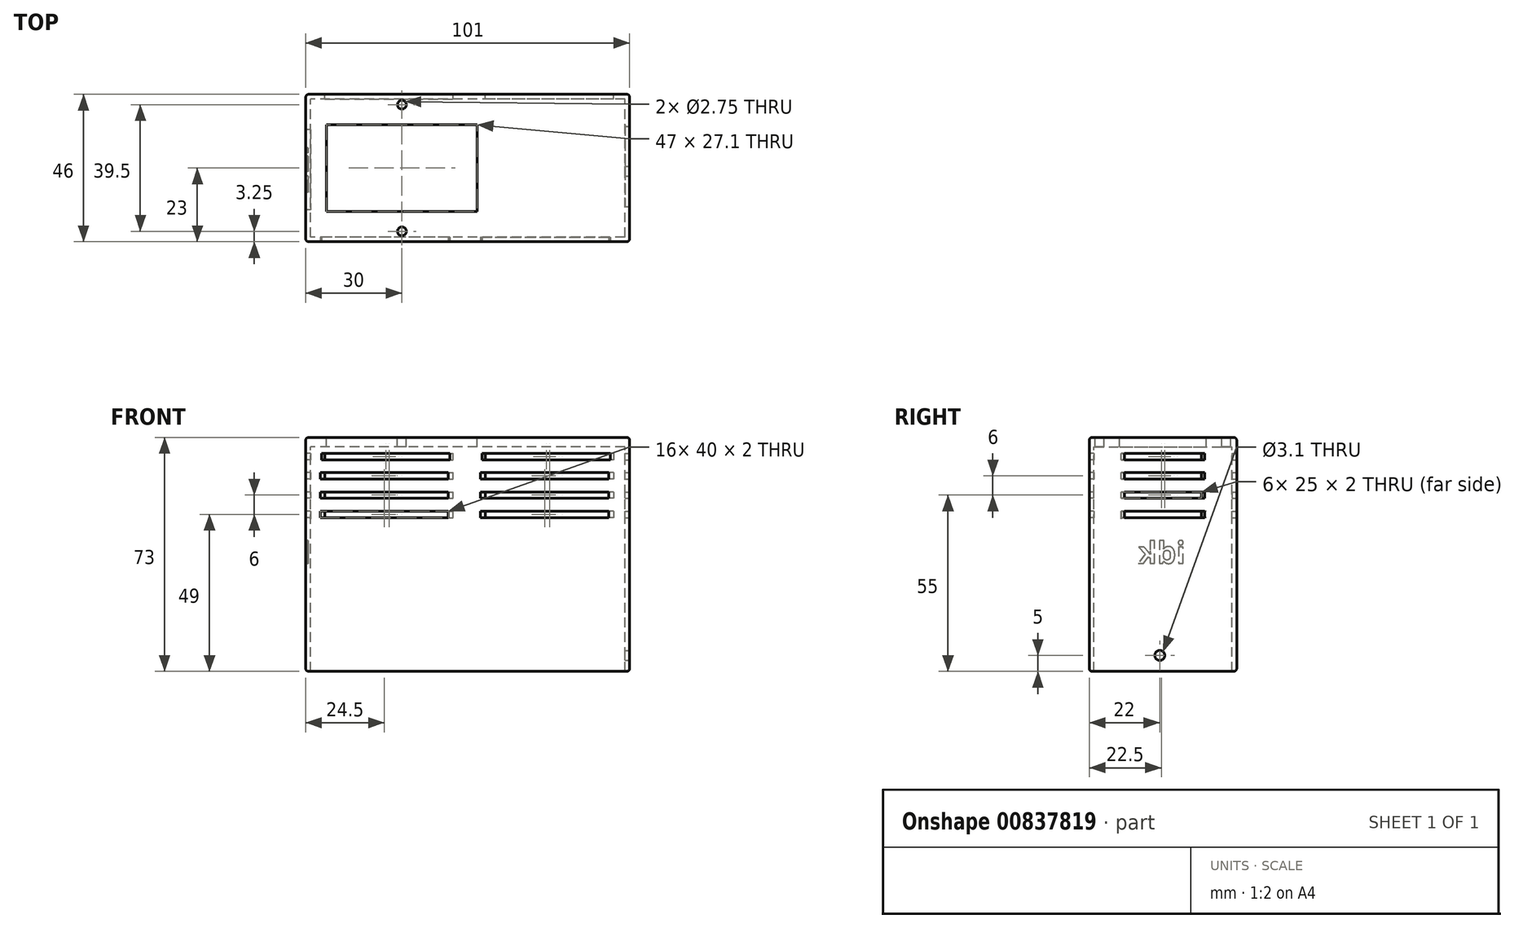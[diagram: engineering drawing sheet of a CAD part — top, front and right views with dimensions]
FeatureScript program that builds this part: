
annotation { "Feature Type Name" : "Feature", "Feature Type Description" : "" }
export const myFeature = defineFeature(function(context is Context, id is Id, definition is map)
    precondition{}
    {
        {
            var Q0;
            Q0=qCreatedBy(makeId("Top.planeOp"),FACE);
            var sketch = newSketch(context, id + "F0", { "sketchPlane" : qUnion([Q0])});
            skLineSegment(sketch, "E0.bottom", {"start": v(49, -21.5) * mm, "end": v(-49, -21.5) * mm});
            skLineSegment(sketch, "E0.top", {"start": v(49, 21.5) * mm, "end": v(-49, 21.5) * mm});
            skLineSegment(sketch, "E0.left", {"start": v(49, -21.5) * mm, "end": v(49, 21.5) * mm});
            skLineSegment(sketch, "E0.right", {"start": v(-49, -21.5) * mm, "end": v(-49, 21.5) * mm});
            skPoint(sketch, "E0.middle", {"position": v(0, 0) * mm});
            skLineSegment(sketch, "E1.bottom", {"start": v(50.5, -23) * mm, "end": v(-50.5, -23) * mm});
            skLineSegment(sketch, "E1.top", {"start": v(50.5, 23) * mm, "end": v(-50.5, 23) * mm});
            skLineSegment(sketch, "E1.left", {"start": v(50.5, -23) * mm, "end": v(50.5, 23) * mm});
            skLineSegment(sketch, "E1.right", {"start": v(-50.5, -23) * mm, "end": v(-50.5, 23) * mm});
            skLineSegment(sketch, "E2.bottom", {"start": v(3, -13.55) * mm, "end": v(-44, -13.55) * mm});
            skLineSegment(sketch, "E2.top", {"start": v(3, 13.55) * mm, "end": v(-44, 13.55) * mm});
            skLineSegment(sketch, "E2.left", {"start": v(3, -13.55) * mm, "end": v(3, 13.55) * mm});
            skLineSegment(sketch, "E2.right", {"start": v(-44, -13.55) * mm, "end": v(-44, 13.55) * mm});
            skPoint(sketch, "E2.middle", {"position": v(-20.5, 0) * mm});
            skLineSegment(sketch, "E3.bottom", {"start": v(39, -10) * mm, "end": v(26, -10) * mm});
            skLineSegment(sketch, "E3.top", {"start": v(39, 10) * mm, "end": v(26, 10) * mm});
            skLineSegment(sketch, "E3.left", {"start": v(39, -10) * mm, "end": v(39, 10) * mm});
            skLineSegment(sketch, "E3.right", {"start": v(26, -10) * mm, "end": v(26, 10) * mm});
            skPoint(sketch, "E3.middle", {"position": v(32.5, 0) * mm});
            skCircle(sketch, "E4", {"center": v(-20.5, -19.75) * mm, "radius": 1.38 * mm});
            skCircle(sketch, "E5", {"center": v(-20.5, 19.75) * mm, "radius": 1.38 * mm});
            skSolve(sketch);
        }
        {
            var Q0;
            Q0=makeQuery(id+"F0.imprint","IMPRINT",FACE,{"disambiguationData":[TD([[makeQuery(id+"F0.imprint","IMPRINT",EDGE,{"derivedFrom":sQuery(id+"F0.wireOp",EDGE,"E0.bottom")}),1.0]])]});
            extrude(context, id + "F1", {"entities" : qUnion([Q0]), "oppositeDirection" : true, "depth" : 73 * mm, "offsetDistance" : 25 * mm});
        }
        {
            var Q0;
            Q0=makeQuery(id+"F0.imprint","IMPRINT",FACE,{"disambiguationData":[TD([[makeQuery(id+"F0.imprint","IMPRINT",EDGE,{"derivedFrom":sQuery(id+"F0.wireOp",EDGE,"E0.bottom")}),-1.0]])]});
            extrude(context, id + "F2", {"entities" : qUnion([Q0]), "operationType" : NewBodyOperationType.ADD, "oppositeDirection" : true, "depth" : 3 * mm, "offsetDistance" : 25 * mm});
        }
        {
            var Q0;
            Q0=qCreatedBy(makeId("Right.planeOp"),FACE);
            cPlane(context, id + "F3", {"entities" : qUnion([Q0]), "cplaneType" : CPlaneType.OFFSET, "offset" : 49 * mm, "width" : 150 * mm, "height" : 150 * mm});
        }
        {
            var Q0;
            Q0=makeQuery(id+"F1.opExtrude","SWEPT_FACE",FACE,{"disambiguationData":[OSD([sQuery(id+"F0.wireOp",EDGE,"E1.left")])]});
            var sketch = newSketch(context, id + "F4", { "sketchPlane" : qUnion([Q0])});
            skCircle(sketch, "E6", {"center": v(-1, -68) * mm, "radius": 1.55 * mm});
            skSolve(sketch);
        }
        {
            var Q0;
            Q0=makeQuery(id+"F4.imprint","IMPRINT",FACE,{"disambiguationData":[TD([[makeQuery(id+"F4.imprint","IMPRINT",EDGE,{"derivedFrom":sQuery(id+"F4.wireOp",EDGE,"E6")}),1.0]])]});
            extrude(context, id + "F5", {"entities" : qUnion([Q0]), "operationType" : NewBodyOperationType.REMOVE, "oppositeDirection" : true, "depth" : 3 * mm, "offsetDistance" : 25 * mm});
        }
        {
            var Q0;
            Q0=makeQuery(id+"F1.opExtrude","CAP_EDGE",EDGE,{"disambiguationData":[OSD([sQuery(id+"F0.wireOp",EDGE,"E1.bottom")])],"isStart":false});
            var Q1;
            Q1=makeQuery(id+"F1.opExtrude","CAP_EDGE",EDGE,{"disambiguationData":[OSD([sQuery(id+"F0.wireOp",EDGE,"E1.left")])],"isStart":false});
            var Q2;
            Q2=makeQuery(id+"F1.opExtrude","CAP_EDGE",EDGE,{"disambiguationData":[OSD([sQuery(id+"F0.wireOp",EDGE,"E1.top")])],"isStart":false});
            var Q3;
            Q3=makeQuery(id+"F1.opExtrude","CAP_EDGE",EDGE,{"disambiguationData":[OSD([sQuery(id+"F0.wireOp",EDGE,"E1.right")])],"isStart":false});
            var Q4;
            Q4=makeQuery(id+"F1.opExtrude","SWEPT_EDGE",EDGE,{"disambiguationData":[OSD([sQuery(id+"F0.wireOp",EDGE,"E1.bottom"),sQuery(id+"F0.wireOp",EDGE,"E1.right")])]});
            var Q5;
            Q5=makeQuery(id+"F1.opExtrude","SWEPT_EDGE",EDGE,{"disambiguationData":[OSD([sQuery(id+"F0.wireOp",EDGE,"E1.top"),sQuery(id+"F0.wireOp",EDGE,"E1.right")])]});
            var Q6;
            Q6=makeQuery(id+"F1.opExtrude","SWEPT_EDGE",EDGE,{"disambiguationData":[OSD([sQuery(id+"F0.wireOp",EDGE,"E1.bottom"),sQuery(id+"F0.wireOp",EDGE,"E1.left")])]});
            var Q7;
            Q7=makeQuery(id+"F1.opExtrude","SWEPT_EDGE",EDGE,{"disambiguationData":[OSD([sQuery(id+"F0.wireOp",EDGE,"E1.top"),sQuery(id+"F0.wireOp",EDGE,"E1.left")])]});
            var Q8;
            Q8=makeQuery(id+"F1.opExtrude","CAP_EDGE",EDGE,{"disambiguationData":[OSD([sQuery(id+"F0.wireOp",EDGE,"E1.bottom")])],"isStart":true});
            var Q9;
            Q9=makeQuery(id+"F1.opExtrude","CAP_EDGE",EDGE,{"disambiguationData":[OSD([sQuery(id+"F0.wireOp",EDGE,"E1.left")])],"isStart":true});
            var Q10;
            Q10=makeQuery(id+"F1.opExtrude","CAP_EDGE",EDGE,{"disambiguationData":[OSD([sQuery(id+"F0.wireOp",EDGE,"E1.top")])],"isStart":true});
            var Q11;
            Q11=makeQuery(id+"F1.opExtrude","CAP_EDGE",EDGE,{"disambiguationData":[OSD([sQuery(id+"F0.wireOp",EDGE,"E1.right")])],"isStart":true});
            var Q12;
            Q12=makeQuery(id+"F5.boolean.opBoolean","COPY",EDGE,{"derivedFrom":makeQuery(id+"F5.opExtrude","CAP_EDGE",EDGE,{"disambiguationData":[OSD([sQuery(id+"F4.wireOp",EDGE,"E6")])],"isStart":true})});
            fillet(context, id + "F6", {"entities" : qUnion([Q0, Q1, Q2, Q3, Q4, Q5, Q6, Q7, Q8, Q9, Q10, Q11, Q12]), "radius" : 1 * mm, "tangentPropagation" : true, "allowEdgeOverflow" : false});
        }
        {
            var Q0;
            Q0=makeQuery(id+"F1.opExtrude","SWEPT_FACE",FACE,{"disambiguationData":[OSD([sQuery(id+"F0.wireOp",EDGE,"E1.bottom")])]});
            var sketch = newSketch(context, id + "F7", { "sketchPlane" : qUnion([Q0])});
            skLineSegment(sketch, "E7.bottom", {"start": v(44.5, -7) * mm, "end": v(4.5, -7) * mm});
            skLineSegment(sketch, "E7.top", {"start": v(44.5, -5) * mm, "end": v(4.5, -5) * mm});
            skLineSegment(sketch, "E7.left", {"start": v(44.5, -7) * mm, "end": v(44.5, -5) * mm});
            skLineSegment(sketch, "E7.right", {"start": v(4.5, -7) * mm, "end": v(4.5, -5) * mm});
            skPoint(sketch, "E7.middle", {"position": v(24.5, -6) * mm});
            skLineSegment(sketch, "E8.bottom", {"start": v(-45.5, -5) * mm, "end": v(-5.5, -5) * mm});
            skLineSegment(sketch, "E8.top", {"start": v(-45.5, -7) * mm, "end": v(-5.5, -7) * mm});
            skLineSegment(sketch, "E8.left", {"start": v(-45.5, -5) * mm, "end": v(-45.5, -7) * mm});
            skLineSegment(sketch, "E8.right", {"start": v(-5.5, -5) * mm, "end": v(-5.5, -7) * mm});
            skPoint(sketch, "E8.middle", {"position": v(-25.5, -6) * mm});
            skLineSegment(sketch, "E9.bottom", {"start": v(44, -13) * mm, "end": v(4, -13) * mm});
            skLineSegment(sketch, "E9.top", {"start": v(44, -11) * mm, "end": v(4, -11) * mm});
            skLineSegment(sketch, "E9.left", {"start": v(44, -13) * mm, "end": v(44, -11) * mm});
            skLineSegment(sketch, "E9.right", {"start": v(4, -13) * mm, "end": v(4, -11) * mm});
            skPoint(sketch, "E9.middle", {"position": v(24, -12) * mm});
            skLineSegment(sketch, "E10.bottom", {"start": v(-46, -11) * mm, "end": v(-6, -11) * mm});
            skLineSegment(sketch, "E10.top", {"start": v(-46, -13) * mm, "end": v(-6, -13) * mm});
            skLineSegment(sketch, "E10.left", {"start": v(-46, -11) * mm, "end": v(-46, -13) * mm});
            skLineSegment(sketch, "E10.right", {"start": v(-6, -11) * mm, "end": v(-6, -13) * mm});
            skPoint(sketch, "E10.middle", {"position": v(-26, -12) * mm});
            skLineSegment(sketch, "E11.bottom", {"start": v(44, -19) * mm, "end": v(4, -19) * mm});
            skLineSegment(sketch, "E11.top", {"start": v(44, -17) * mm, "end": v(4, -17) * mm});
            skLineSegment(sketch, "E11.left", {"start": v(44, -19) * mm, "end": v(44, -17) * mm});
            skLineSegment(sketch, "E11.right", {"start": v(4, -19) * mm, "end": v(4, -17) * mm});
            skPoint(sketch, "E11.middle", {"position": v(24, -18) * mm});
            skLineSegment(sketch, "E12.bottom", {"start": v(-46, -17) * mm, "end": v(-6, -17) * mm});
            skLineSegment(sketch, "E12.top", {"start": v(-46, -19) * mm, "end": v(-6, -19) * mm});
            skLineSegment(sketch, "E12.left", {"start": v(-46, -17) * mm, "end": v(-46, -19) * mm});
            skLineSegment(sketch, "E12.right", {"start": v(-6, -17) * mm, "end": v(-6, -19) * mm});
            skPoint(sketch, "E12.middle", {"position": v(-26, -18) * mm});
            skLineSegment(sketch, "E13.bottom", {"start": v(44, -25) * mm, "end": v(4, -25) * mm});
            skLineSegment(sketch, "E13.top", {"start": v(44, -23) * mm, "end": v(4, -23) * mm});
            skLineSegment(sketch, "E13.left", {"start": v(44, -25) * mm, "end": v(44, -23) * mm});
            skLineSegment(sketch, "E13.right", {"start": v(4, -25) * mm, "end": v(4, -23) * mm});
            skPoint(sketch, "E13.middle", {"position": v(24, -24) * mm});
            skLineSegment(sketch, "E14.bottom", {"start": v(-46, -23) * mm, "end": v(-6, -23) * mm});
            skLineSegment(sketch, "E14.top", {"start": v(-46, -25) * mm, "end": v(-6, -25) * mm});
            skLineSegment(sketch, "E14.left", {"start": v(-46, -23) * mm, "end": v(-46, -25) * mm});
            skLineSegment(sketch, "E14.right", {"start": v(-6, -23) * mm, "end": v(-6, -25) * mm});
            skPoint(sketch, "E14.middle", {"position": v(-26, -24) * mm});
            skSolve(sketch);
        }
        {
            var Q0;
            Q0=makeQuery(id+"F1.opExtrude","SWEPT_FACE",FACE,{"disambiguationData":[OSD([sQuery(id+"F0.wireOp",EDGE,"E1.top")])]});
            var sketch = newSketch(context, id + "F8", { "sketchPlane" : qUnion([Q0])});
            skLineSegment(sketch, "E15.bottom", {"start": v(44.5, -7) * mm, "end": v(4.5, -7) * mm});
            skLineSegment(sketch, "E15.top", {"start": v(44.5, -5) * mm, "end": v(4.5, -5) * mm});
            skLineSegment(sketch, "E15.left", {"start": v(44.5, -7) * mm, "end": v(44.5, -5) * mm});
            skLineSegment(sketch, "E15.right", {"start": v(4.5, -7) * mm, "end": v(4.5, -5) * mm});
            skPoint(sketch, "E15.middle", {"position": v(24.5, -6) * mm});
            skLineSegment(sketch, "E16.bottom", {"start": v(-45.5, -5) * mm, "end": v(-5.5, -5) * mm});
            skLineSegment(sketch, "E16.top", {"start": v(-45.5, -7) * mm, "end": v(-5.5, -7) * mm});
            skLineSegment(sketch, "E16.left", {"start": v(-45.5, -5) * mm, "end": v(-45.5, -7) * mm});
            skLineSegment(sketch, "E16.right", {"start": v(-5.5, -5) * mm, "end": v(-5.5, -7) * mm});
            skPoint(sketch, "E16.middle", {"position": v(-25.5, -6) * mm});
            skLineSegment(sketch, "E17.bottom", {"start": v(44.5, -13) * mm, "end": v(4.5, -13) * mm});
            skLineSegment(sketch, "E17.top", {"start": v(44.5, -11) * mm, "end": v(4.5, -11) * mm});
            skLineSegment(sketch, "E17.left", {"start": v(44.5, -13) * mm, "end": v(44.5, -11) * mm});
            skLineSegment(sketch, "E17.right", {"start": v(4.5, -13) * mm, "end": v(4.5, -11) * mm});
            skPoint(sketch, "E17.middle", {"position": v(24.5, -12) * mm});
            skLineSegment(sketch, "E18.bottom", {"start": v(-45.5, -11) * mm, "end": v(-5.5, -11) * mm});
            skLineSegment(sketch, "E18.top", {"start": v(-45.5, -13) * mm, "end": v(-5.5, -13) * mm});
            skLineSegment(sketch, "E18.left", {"start": v(-45.5, -11) * mm, "end": v(-45.5, -13) * mm});
            skLineSegment(sketch, "E18.right", {"start": v(-5.5, -11) * mm, "end": v(-5.5, -13) * mm});
            skPoint(sketch, "E18.middle", {"position": v(-25.5, -12) * mm});
            skLineSegment(sketch, "E19.bottom", {"start": v(44.5, -19) * mm, "end": v(4.5, -19) * mm});
            skLineSegment(sketch, "E19.top", {"start": v(44.5, -17) * mm, "end": v(4.5, -17) * mm});
            skLineSegment(sketch, "E19.left", {"start": v(44.5, -19) * mm, "end": v(44.5, -17) * mm});
            skLineSegment(sketch, "E19.right", {"start": v(4.5, -19) * mm, "end": v(4.5, -17) * mm});
            skPoint(sketch, "E19.middle", {"position": v(24.5, -18) * mm});
            skLineSegment(sketch, "E20.bottom", {"start": v(-45.5, -17) * mm, "end": v(-5.5, -17) * mm});
            skLineSegment(sketch, "E20.top", {"start": v(-45.5, -19) * mm, "end": v(-5.5, -19) * mm});
            skLineSegment(sketch, "E20.left", {"start": v(-45.5, -17) * mm, "end": v(-45.5, -19) * mm});
            skLineSegment(sketch, "E20.right", {"start": v(-5.5, -17) * mm, "end": v(-5.5, -19) * mm});
            skPoint(sketch, "E20.middle", {"position": v(-25.5, -18) * mm});
            skLineSegment(sketch, "E21.bottom", {"start": v(44.5, -25) * mm, "end": v(4.5, -25) * mm});
            skLineSegment(sketch, "E21.top", {"start": v(44.5, -23) * mm, "end": v(4.5, -23) * mm});
            skLineSegment(sketch, "E21.left", {"start": v(44.5, -25) * mm, "end": v(44.5, -23) * mm});
            skLineSegment(sketch, "E21.right", {"start": v(4.5, -25) * mm, "end": v(4.5, -23) * mm});
            skPoint(sketch, "E21.middle", {"position": v(24.5, -24) * mm});
            skLineSegment(sketch, "E22.bottom", {"start": v(-45.5, -23) * mm, "end": v(-5.5, -23) * mm});
            skLineSegment(sketch, "E22.top", {"start": v(-45.5, -25) * mm, "end": v(-5.5, -25) * mm});
            skLineSegment(sketch, "E22.left", {"start": v(-45.5, -23) * mm, "end": v(-45.5, -25) * mm});
            skLineSegment(sketch, "E22.right", {"start": v(-5.5, -23) * mm, "end": v(-5.5, -25) * mm});
            skPoint(sketch, "E22.middle", {"position": v(-25.5, -24) * mm});
            skSolve(sketch);
        }
        {
            var Q0;
            Q0=qSketchRegion(id+"F8",true);
            extrude(context, id + "F9", {"entities" : qUnion([Q0]), "operationType" : NewBodyOperationType.REMOVE, "oppositeDirection" : true, "depth" : 3 * mm, "offsetDistance" : 25 * mm});
        }
        {
            var Q0;
            Q0=qSketchRegion(id+"F7",true);
            extrude(context, id + "F10", {"entities" : qUnion([Q0]), "operationType" : NewBodyOperationType.REMOVE, "oppositeDirection" : true, "depth" : 3 * mm, "offsetDistance" : 25 * mm});
        }
        {
            var Q0;
            Q0=makeQuery(id+"F1.opExtrude","SWEPT_FACE",FACE,{"disambiguationData":[OSD([sQuery(id+"F0.wireOp",EDGE,"E1.left")])]});
            var sketch = newSketch(context, id + "F11", { "sketchPlane" : qUnion([Q0])});
            skLineSegment(sketch, "E23.bottom", {"start": v(13, -7) * mm, "end": v(-12, -7) * mm});
            skLineSegment(sketch, "E23.top", {"start": v(13, -5) * mm, "end": v(-12, -5) * mm});
            skLineSegment(sketch, "E23.left", {"start": v(13, -7) * mm, "end": v(13, -5) * mm});
            skLineSegment(sketch, "E23.right", {"start": v(-12, -7) * mm, "end": v(-12, -5) * mm});
            skPoint(sketch, "E23.middle", {"position": v(0.5, -6) * mm});
            skLineSegment(sketch, "E24.bottom", {"start": v(13, -13) * mm, "end": v(-12, -13) * mm});
            skLineSegment(sketch, "E24.top", {"start": v(13, -11) * mm, "end": v(-12, -11) * mm});
            skLineSegment(sketch, "E24.left", {"start": v(13, -13) * mm, "end": v(13, -11) * mm});
            skLineSegment(sketch, "E24.right", {"start": v(-12, -13) * mm, "end": v(-12, -11) * mm});
            skPoint(sketch, "E24.middle", {"position": v(0.5, -12) * mm});
            skLineSegment(sketch, "E25.bottom", {"start": v(13, -19) * mm, "end": v(-12, -19) * mm});
            skLineSegment(sketch, "E25.top", {"start": v(13, -17) * mm, "end": v(-12, -17) * mm});
            skLineSegment(sketch, "E25.left", {"start": v(13, -19) * mm, "end": v(13, -17) * mm});
            skLineSegment(sketch, "E25.right", {"start": v(-12, -19) * mm, "end": v(-12, -17) * mm});
            skPoint(sketch, "E25.middle", {"position": v(0.5, -18) * mm});
            skLineSegment(sketch, "E26.bottom", {"start": v(13, -25) * mm, "end": v(-12, -25) * mm});
            skLineSegment(sketch, "E26.top", {"start": v(13, -23) * mm, "end": v(-12, -23) * mm});
            skLineSegment(sketch, "E26.left", {"start": v(13, -25) * mm, "end": v(13, -23) * mm});
            skLineSegment(sketch, "E26.right", {"start": v(-12, -25) * mm, "end": v(-12, -23) * mm});
            skPoint(sketch, "E26.middle", {"position": v(0.5, -24) * mm});
            skSolve(sketch);
        }
        {
            var Q0;
            Q0=qSketchRegion(id+"F11",true);
            extrude(context, id + "F12", {"entities" : qUnion([Q0]), "operationType" : NewBodyOperationType.REMOVE, "oppositeDirection" : true, "depth" : 3 * mm, "offsetDistance" : 25 * mm});
        }
        {
            var Q0;
            Q0=makeQuery(id+"F1.opExtrude","SWEPT_FACE",FACE,{"disambiguationData":[OSD([sQuery(id+"F0.wireOp",EDGE,"E1.right")])]});
            var sketch = newSketch(context, id + "F13", { "sketchPlane" : qUnion([Q0])});
            skLineSegment(sketch, "E27.bottom", {"start": v(13, -7) * mm, "end": v(-12, -7) * mm});
            skLineSegment(sketch, "E27.top", {"start": v(13, -5) * mm, "end": v(-12, -5) * mm});
            skLineSegment(sketch, "E27.left", {"start": v(13, -7) * mm, "end": v(13, -5) * mm});
            skLineSegment(sketch, "E27.right", {"start": v(-12, -7) * mm, "end": v(-12, -5) * mm});
            skPoint(sketch, "E27.middle", {"position": v(0.5, -6) * mm});
            skLineSegment(sketch, "E28.bottom", {"start": v(13, -13) * mm, "end": v(-12, -13) * mm});
            skLineSegment(sketch, "E28.top", {"start": v(13, -11) * mm, "end": v(-12, -11) * mm});
            skLineSegment(sketch, "E28.left", {"start": v(13, -13) * mm, "end": v(13, -11) * mm});
            skLineSegment(sketch, "E28.right", {"start": v(-12, -13) * mm, "end": v(-12, -11) * mm});
            skPoint(sketch, "E28.middle", {"position": v(0.5, -12) * mm});
            skLineSegment(sketch, "E29.bottom", {"start": v(13, -19) * mm, "end": v(-12, -19) * mm});
            skLineSegment(sketch, "E29.top", {"start": v(13, -17) * mm, "end": v(-12, -17) * mm});
            skLineSegment(sketch, "E29.left", {"start": v(13, -19) * mm, "end": v(13, -17) * mm});
            skLineSegment(sketch, "E29.right", {"start": v(-12, -19) * mm, "end": v(-12, -17) * mm});
            skPoint(sketch, "E29.middle", {"position": v(0.5, -18) * mm});
            skLineSegment(sketch, "E30.bottom", {"start": v(13, -25) * mm, "end": v(-12, -25) * mm});
            skLineSegment(sketch, "E30.top", {"start": v(13, -23) * mm, "end": v(-12, -23) * mm});
            skLineSegment(sketch, "E30.left", {"start": v(13, -25) * mm, "end": v(13, -23) * mm});
            skLineSegment(sketch, "E30.right", {"start": v(-12, -25) * mm, "end": v(-12, -23) * mm});
            skPoint(sketch, "E30.middle", {"position": v(0.5, -24) * mm});
            skSolve(sketch);
        }
        {
            var Q0;
            Q0=qSketchRegion(id+"F13",true);
            extrude(context, id + "F14", {"entities" : qUnion([Q0]), "operationType" : NewBodyOperationType.REMOVE, "oppositeDirection" : true, "depth" : 3 * mm, "offsetDistance" : 25 * mm});
        }
        {
            var Q0;
            Q0=makeQuery(id+"F10.boolean.opBoolean","COPY",EDGE,{"derivedFrom":makeQuery(id+"F10.opExtrude","CAP_EDGE",EDGE,{"disambiguationData":[OSD([sQuery(id+"F7.wireOp",EDGE,"E13.left")])],"isStart":true})});
            var Q1;
            Q1=makeQuery(id+"F10.boolean.opBoolean","COPY",EDGE,{"derivedFrom":makeQuery(id+"F10.opExtrude","CAP_EDGE",EDGE,{"disambiguationData":[OSD([sQuery(id+"F7.wireOp",EDGE,"E13.bottom")])],"isStart":true})});
            var Q2;
            Q2=makeQuery(id+"F10.boolean.opBoolean","COPY",EDGE,{"derivedFrom":makeQuery(id+"F10.opExtrude","CAP_EDGE",EDGE,{"disambiguationData":[OSD([sQuery(id+"F7.wireOp",EDGE,"E13.top")])],"isStart":true})});
            var Q3;
            Q3=makeQuery(id+"F10.boolean.opBoolean","COPY",EDGE,{"derivedFrom":makeQuery(id+"F10.opExtrude","CAP_EDGE",EDGE,{"disambiguationData":[OSD([sQuery(id+"F7.wireOp",EDGE,"E13.right")])],"isStart":true})});
            var Q4;
            Q4=makeQuery(id+"F10.boolean.opBoolean","COPY",EDGE,{"derivedFrom":makeQuery(id+"F10.opExtrude","CAP_EDGE",EDGE,{"disambiguationData":[OSD([sQuery(id+"F7.wireOp",EDGE,"E11.bottom")])],"isStart":true})});
            var Q5;
            Q5=makeQuery(id+"F10.boolean.opBoolean","COPY",EDGE,{"derivedFrom":makeQuery(id+"F10.opExtrude","CAP_EDGE",EDGE,{"disambiguationData":[OSD([sQuery(id+"F7.wireOp",EDGE,"E11.left")])],"isStart":true})});
            var Q6;
            Q6=makeQuery(id+"F10.boolean.opBoolean","COPY",EDGE,{"derivedFrom":makeQuery(id+"F10.opExtrude","CAP_EDGE",EDGE,{"disambiguationData":[OSD([sQuery(id+"F7.wireOp",EDGE,"E11.top")])],"isStart":true})});
            var Q7;
            Q7=makeQuery(id+"F10.boolean.opBoolean","COPY",EDGE,{"derivedFrom":makeQuery(id+"F10.opExtrude","CAP_EDGE",EDGE,{"disambiguationData":[OSD([sQuery(id+"F7.wireOp",EDGE,"E11.right")])],"isStart":true})});
            var Q8;
            Q8=makeQuery(id+"F10.boolean.opBoolean","COPY",EDGE,{"derivedFrom":makeQuery(id+"F10.opExtrude","CAP_EDGE",EDGE,{"disambiguationData":[OSD([sQuery(id+"F7.wireOp",EDGE,"E9.right")])],"isStart":true})});
            var Q9;
            Q9=makeQuery(id+"F10.boolean.opBoolean","COPY",EDGE,{"derivedFrom":makeQuery(id+"F10.opExtrude","CAP_EDGE",EDGE,{"disambiguationData":[OSD([sQuery(id+"F7.wireOp",EDGE,"E9.bottom")])],"isStart":true})});
            var Q10;
            Q10=makeQuery(id+"F10.boolean.opBoolean","COPY",EDGE,{"derivedFrom":makeQuery(id+"F10.opExtrude","CAP_EDGE",EDGE,{"disambiguationData":[OSD([sQuery(id+"F7.wireOp",EDGE,"E9.left")])],"isStart":true})});
            var Q11;
            Q11=makeQuery(id+"F10.boolean.opBoolean","COPY",EDGE,{"derivedFrom":makeQuery(id+"F10.opExtrude","CAP_EDGE",EDGE,{"disambiguationData":[OSD([sQuery(id+"F7.wireOp",EDGE,"E9.top")])],"isStart":true})});
            var Q12;
            Q12=makeQuery(id+"F10.boolean.opBoolean","COPY",EDGE,{"derivedFrom":makeQuery(id+"F10.opExtrude","CAP_EDGE",EDGE,{"disambiguationData":[OSD([sQuery(id+"F7.wireOp",EDGE,"E7.bottom")])],"isStart":true})});
            var Q13;
            Q13=makeQuery(id+"F10.boolean.opBoolean","COPY",EDGE,{"derivedFrom":makeQuery(id+"F10.opExtrude","CAP_EDGE",EDGE,{"disambiguationData":[OSD([sQuery(id+"F7.wireOp",EDGE,"E7.left")])],"isStart":true})});
            var Q14;
            Q14=makeQuery(id+"F10.boolean.opBoolean","COPY",EDGE,{"derivedFrom":makeQuery(id+"F10.opExtrude","CAP_EDGE",EDGE,{"disambiguationData":[OSD([sQuery(id+"F7.wireOp",EDGE,"E7.top")])],"isStart":true})});
            var Q15;
            Q15=makeQuery(id+"F10.boolean.opBoolean","COPY",EDGE,{"derivedFrom":makeQuery(id+"F10.opExtrude","CAP_EDGE",EDGE,{"disambiguationData":[OSD([sQuery(id+"F7.wireOp",EDGE,"E7.right")])],"isStart":true})});
            var Q16;
            Q16=makeQuery(id+"F10.boolean.opBoolean","COPY",EDGE,{"derivedFrom":makeQuery(id+"F10.opExtrude","CAP_EDGE",EDGE,{"disambiguationData":[OSD([sQuery(id+"F7.wireOp",EDGE,"E14.right")])],"isStart":true})});
            var Q17;
            Q17=makeQuery(id+"F10.boolean.opBoolean","COPY",EDGE,{"derivedFrom":makeQuery(id+"F10.opExtrude","CAP_EDGE",EDGE,{"disambiguationData":[OSD([sQuery(id+"F7.wireOp",EDGE,"E14.top")])],"isStart":true})});
            var Q18;
            Q18=makeQuery(id+"F10.boolean.opBoolean","COPY",EDGE,{"derivedFrom":makeQuery(id+"F10.opExtrude","CAP_EDGE",EDGE,{"disambiguationData":[OSD([sQuery(id+"F7.wireOp",EDGE,"E14.left")])],"isStart":true})});
            var Q19;
            Q19=makeQuery(id+"F10.boolean.opBoolean","COPY",EDGE,{"derivedFrom":makeQuery(id+"F10.opExtrude","CAP_EDGE",EDGE,{"disambiguationData":[OSD([sQuery(id+"F7.wireOp",EDGE,"E14.bottom")])],"isStart":true})});
            var Q20;
            Q20=makeQuery(id+"F10.boolean.opBoolean","COPY",EDGE,{"derivedFrom":makeQuery(id+"F10.opExtrude","CAP_EDGE",EDGE,{"disambiguationData":[OSD([sQuery(id+"F7.wireOp",EDGE,"E12.top")])],"isStart":true})});
            var Q21;
            Q21=makeQuery(id+"F10.boolean.opBoolean","COPY",EDGE,{"derivedFrom":makeQuery(id+"F10.opExtrude","CAP_EDGE",EDGE,{"disambiguationData":[OSD([sQuery(id+"F7.wireOp",EDGE,"E12.right")])],"isStart":true})});
            var Q22;
            Q22=makeQuery(id+"F10.boolean.opBoolean","COPY",EDGE,{"derivedFrom":makeQuery(id+"F10.opExtrude","CAP_EDGE",EDGE,{"disambiguationData":[OSD([sQuery(id+"F7.wireOp",EDGE,"E12.bottom")])],"isStart":true})});
            var Q23;
            Q23=makeQuery(id+"F10.boolean.opBoolean","COPY",EDGE,{"derivedFrom":makeQuery(id+"F10.opExtrude","CAP_EDGE",EDGE,{"disambiguationData":[OSD([sQuery(id+"F7.wireOp",EDGE,"E12.left")])],"isStart":true})});
            var Q24;
            Q24=makeQuery(id+"F10.boolean.opBoolean","COPY",EDGE,{"derivedFrom":makeQuery(id+"F10.opExtrude","CAP_EDGE",EDGE,{"disambiguationData":[OSD([sQuery(id+"F7.wireOp",EDGE,"E10.left")])],"isStart":true})});
            var Q25;
            Q25=makeQuery(id+"F10.boolean.opBoolean","COPY",EDGE,{"derivedFrom":makeQuery(id+"F10.opExtrude","CAP_EDGE",EDGE,{"disambiguationData":[OSD([sQuery(id+"F7.wireOp",EDGE,"E10.top")])],"isStart":true})});
            var Q26;
            Q26=makeQuery(id+"F10.boolean.opBoolean","COPY",EDGE,{"derivedFrom":makeQuery(id+"F10.opExtrude","CAP_EDGE",EDGE,{"disambiguationData":[OSD([sQuery(id+"F7.wireOp",EDGE,"E10.right")])],"isStart":true})});
            var Q27;
            Q27=makeQuery(id+"F10.boolean.opBoolean","COPY",EDGE,{"derivedFrom":makeQuery(id+"F10.opExtrude","CAP_EDGE",EDGE,{"disambiguationData":[OSD([sQuery(id+"F7.wireOp",EDGE,"E10.bottom")])],"isStart":true})});
            var Q28;
            Q28=makeQuery(id+"F10.boolean.opBoolean","COPY",EDGE,{"derivedFrom":makeQuery(id+"F10.opExtrude","CAP_EDGE",EDGE,{"disambiguationData":[OSD([sQuery(id+"F7.wireOp",EDGE,"E8.top")])],"isStart":true})});
            var Q29;
            Q29=makeQuery(id+"F10.boolean.opBoolean","COPY",EDGE,{"derivedFrom":makeQuery(id+"F10.opExtrude","CAP_EDGE",EDGE,{"disambiguationData":[OSD([sQuery(id+"F7.wireOp",EDGE,"E8.right")])],"isStart":true})});
            var Q30;
            Q30=makeQuery(id+"F10.boolean.opBoolean","COPY",EDGE,{"derivedFrom":makeQuery(id+"F10.opExtrude","CAP_EDGE",EDGE,{"disambiguationData":[OSD([sQuery(id+"F7.wireOp",EDGE,"E8.bottom")])],"isStart":true})});
            var Q31;
            Q31=makeQuery(id+"F10.boolean.opBoolean","COPY",EDGE,{"derivedFrom":makeQuery(id+"F10.opExtrude","CAP_EDGE",EDGE,{"disambiguationData":[OSD([sQuery(id+"F7.wireOp",EDGE,"E8.left")])],"isStart":true})});
            var Q32;
            Q32=makeQuery(id+"F12.boolean.opBoolean","COPY",EDGE,{"derivedFrom":makeQuery(id+"F12.opExtrude","CAP_EDGE",EDGE,{"disambiguationData":[OSD([sQuery(id+"F11.wireOp",EDGE,"E26.bottom")])],"isStart":true})});
            var Q33;
            Q33=makeQuery(id+"F12.boolean.opBoolean","INTERSECT",EDGE,{"derivedFrom":[makeQuery(id+"F1.opExtrude","SWEPT_FACE",FACE,{"disambiguationData":[OSD([sQuery(id+"F0.wireOp",EDGE,"E0.left")])]}),makeQuery(id+"F12.opExtrude","SWEPT_FACE",FACE,{"disambiguationData":[OSD([sQuery(id+"F11.wireOp",EDGE,"E26.left")])]})]});
            var Q34;
            Q34=makeQuery(id+"F12.boolean.opBoolean","COPY",EDGE,{"derivedFrom":makeQuery(id+"F12.opExtrude","CAP_EDGE",EDGE,{"disambiguationData":[OSD([sQuery(id+"F11.wireOp",EDGE,"E26.top")])],"isStart":true})});
            var Q35;
            Q35=makeQuery(id+"F12.boolean.opBoolean","COPY",EDGE,{"derivedFrom":makeQuery(id+"F12.opExtrude","CAP_EDGE",EDGE,{"disambiguationData":[OSD([sQuery(id+"F11.wireOp",EDGE,"E26.right")])],"isStart":true})});
            var Q36;
            Q36=makeQuery(id+"F12.boolean.opBoolean","COPY",EDGE,{"derivedFrom":makeQuery(id+"F12.opExtrude","CAP_EDGE",EDGE,{"disambiguationData":[OSD([sQuery(id+"F11.wireOp",EDGE,"E25.right")])],"isStart":true})});
            var Q37;
            Q37=makeQuery(id+"F12.boolean.opBoolean","COPY",EDGE,{"derivedFrom":makeQuery(id+"F12.opExtrude","CAP_EDGE",EDGE,{"disambiguationData":[OSD([sQuery(id+"F11.wireOp",EDGE,"E25.bottom")])],"isStart":true})});
            var Q38;
            Q38=makeQuery(id+"F12.boolean.opBoolean","COPY",EDGE,{"derivedFrom":makeQuery(id+"F12.opExtrude","CAP_EDGE",EDGE,{"disambiguationData":[OSD([sQuery(id+"F11.wireOp",EDGE,"E25.left")])],"isStart":true})});
            var Q39;
            Q39=makeQuery(id+"F12.boolean.opBoolean","COPY",EDGE,{"derivedFrom":makeQuery(id+"F12.opExtrude","CAP_EDGE",EDGE,{"disambiguationData":[OSD([sQuery(id+"F11.wireOp",EDGE,"E25.top")])],"isStart":true})});
            var Q40;
            Q40=makeQuery(id+"F12.boolean.opBoolean","COPY",EDGE,{"derivedFrom":makeQuery(id+"F12.opExtrude","CAP_EDGE",EDGE,{"disambiguationData":[OSD([sQuery(id+"F11.wireOp",EDGE,"E24.left")])],"isStart":true})});
            var Q41;
            Q41=makeQuery(id+"F12.boolean.opBoolean","COPY",EDGE,{"derivedFrom":makeQuery(id+"F12.opExtrude","CAP_EDGE",EDGE,{"disambiguationData":[OSD([sQuery(id+"F11.wireOp",EDGE,"E24.bottom")])],"isStart":true})});
            var Q42;
            Q42=makeQuery(id+"F12.boolean.opBoolean","COPY",EDGE,{"derivedFrom":makeQuery(id+"F12.opExtrude","CAP_EDGE",EDGE,{"disambiguationData":[OSD([sQuery(id+"F11.wireOp",EDGE,"E24.top")])],"isStart":true})});
            var Q43;
            Q43=makeQuery(id+"F12.boolean.opBoolean","COPY",EDGE,{"derivedFrom":makeQuery(id+"F12.opExtrude","CAP_EDGE",EDGE,{"disambiguationData":[OSD([sQuery(id+"F11.wireOp",EDGE,"E24.right")])],"isStart":true})});
            var Q44;
            Q44=makeQuery(id+"F12.boolean.opBoolean","COPY",EDGE,{"derivedFrom":makeQuery(id+"F12.opExtrude","CAP_EDGE",EDGE,{"disambiguationData":[OSD([sQuery(id+"F11.wireOp",EDGE,"E23.right")])],"isStart":true})});
            var Q45;
            Q45=makeQuery(id+"F12.boolean.opBoolean","COPY",EDGE,{"derivedFrom":makeQuery(id+"F12.opExtrude","CAP_EDGE",EDGE,{"disambiguationData":[OSD([sQuery(id+"F11.wireOp",EDGE,"E23.bottom")])],"isStart":true})});
            var Q46;
            Q46=makeQuery(id+"F12.boolean.opBoolean","COPY",EDGE,{"derivedFrom":makeQuery(id+"F12.opExtrude","CAP_EDGE",EDGE,{"disambiguationData":[OSD([sQuery(id+"F11.wireOp",EDGE,"E23.left")])],"isStart":true})});
            var Q47;
            Q47=makeQuery(id+"F12.boolean.opBoolean","COPY",EDGE,{"derivedFrom":makeQuery(id+"F12.opExtrude","CAP_EDGE",EDGE,{"disambiguationData":[OSD([sQuery(id+"F11.wireOp",EDGE,"E23.top")])],"isStart":true})});
            var Q48;
            Q48=makeQuery(id+"F12.boolean.opBoolean","COPY",EDGE,{"derivedFrom":makeQuery(id+"F12.opExtrude","CAP_EDGE",EDGE,{"disambiguationData":[OSD([sQuery(id+"F11.wireOp",EDGE,"E26.left")])],"isStart":true})});
            var Q49;
            Q49=makeQuery(id+"F9.boolean.opBoolean","COPY",EDGE,{"derivedFrom":makeQuery(id+"F9.opExtrude","CAP_EDGE",EDGE,{"disambiguationData":[OSD([sQuery(id+"F8.wireOp",EDGE,"E22.top")])],"isStart":true})});
            var Q50;
            Q50=makeQuery(id+"F9.boolean.opBoolean","COPY",EDGE,{"derivedFrom":makeQuery(id+"F9.opExtrude","CAP_EDGE",EDGE,{"disambiguationData":[OSD([sQuery(id+"F8.wireOp",EDGE,"E22.right")])],"isStart":true})});
            var Q51;
            Q51=makeQuery(id+"F9.boolean.opBoolean","COPY",EDGE,{"derivedFrom":makeQuery(id+"F9.opExtrude","CAP_EDGE",EDGE,{"disambiguationData":[OSD([sQuery(id+"F8.wireOp",EDGE,"E22.left")])],"isStart":true})});
            var Q52;
            Q52=makeQuery(id+"F9.boolean.opBoolean","COPY",EDGE,{"derivedFrom":makeQuery(id+"F9.opExtrude","CAP_EDGE",EDGE,{"disambiguationData":[OSD([sQuery(id+"F8.wireOp",EDGE,"E22.bottom")])],"isStart":true})});
            var Q53;
            Q53=makeQuery(id+"F9.boolean.opBoolean","COPY",EDGE,{"derivedFrom":makeQuery(id+"F9.opExtrude","CAP_EDGE",EDGE,{"disambiguationData":[OSD([sQuery(id+"F8.wireOp",EDGE,"E20.top")])],"isStart":true})});
            var Q54;
            Q54=makeQuery(id+"F9.boolean.opBoolean","COPY",EDGE,{"derivedFrom":makeQuery(id+"F9.opExtrude","CAP_EDGE",EDGE,{"disambiguationData":[OSD([sQuery(id+"F8.wireOp",EDGE,"E20.left")])],"isStart":true})});
            var Q55;
            Q55=makeQuery(id+"F9.boolean.opBoolean","COPY",EDGE,{"derivedFrom":makeQuery(id+"F9.opExtrude","CAP_EDGE",EDGE,{"disambiguationData":[OSD([sQuery(id+"F8.wireOp",EDGE,"E20.bottom")])],"isStart":true})});
            var Q56;
            Q56=makeQuery(id+"F9.boolean.opBoolean","COPY",EDGE,{"derivedFrom":makeQuery(id+"F9.opExtrude","CAP_EDGE",EDGE,{"disambiguationData":[OSD([sQuery(id+"F8.wireOp",EDGE,"E20.right")])],"isStart":true})});
            var Q57;
            Q57=makeQuery(id+"F9.boolean.opBoolean","COPY",EDGE,{"derivedFrom":makeQuery(id+"F9.opExtrude","CAP_EDGE",EDGE,{"disambiguationData":[OSD([sQuery(id+"F8.wireOp",EDGE,"E18.right")])],"isStart":true})});
            var Q58;
            Q58=makeQuery(id+"F9.boolean.opBoolean","COPY",EDGE,{"derivedFrom":makeQuery(id+"F9.opExtrude","CAP_EDGE",EDGE,{"disambiguationData":[OSD([sQuery(id+"F8.wireOp",EDGE,"E18.top")])],"isStart":true})});
            var Q59;
            Q59=makeQuery(id+"F9.boolean.opBoolean","COPY",EDGE,{"derivedFrom":makeQuery(id+"F9.opExtrude","CAP_EDGE",EDGE,{"disambiguationData":[OSD([sQuery(id+"F8.wireOp",EDGE,"E18.bottom")])],"isStart":true})});
            var Q60;
            Q60=makeQuery(id+"F9.boolean.opBoolean","COPY",EDGE,{"derivedFrom":makeQuery(id+"F9.opExtrude","CAP_EDGE",EDGE,{"disambiguationData":[OSD([sQuery(id+"F8.wireOp",EDGE,"E18.left")])],"isStart":true})});
            var Q61;
            Q61=makeQuery(id+"F9.boolean.opBoolean","COPY",EDGE,{"derivedFrom":makeQuery(id+"F9.opExtrude","CAP_EDGE",EDGE,{"disambiguationData":[OSD([sQuery(id+"F8.wireOp",EDGE,"E16.left")])],"isStart":true})});
            var Q62;
            Q62=makeQuery(id+"F9.boolean.opBoolean","COPY",EDGE,{"derivedFrom":makeQuery(id+"F9.opExtrude","CAP_EDGE",EDGE,{"disambiguationData":[OSD([sQuery(id+"F8.wireOp",EDGE,"E16.top")])],"isStart":true})});
            var Q63;
            Q63=makeQuery(id+"F9.boolean.opBoolean","COPY",EDGE,{"derivedFrom":makeQuery(id+"F9.opExtrude","CAP_EDGE",EDGE,{"disambiguationData":[OSD([sQuery(id+"F8.wireOp",EDGE,"E16.bottom")])],"isStart":true})});
            var Q64;
            Q64=makeQuery(id+"F9.boolean.opBoolean","COPY",EDGE,{"derivedFrom":makeQuery(id+"F9.opExtrude","CAP_EDGE",EDGE,{"disambiguationData":[OSD([sQuery(id+"F8.wireOp",EDGE,"E16.right")])],"isStart":true})});
            var Q65;
            Q65=makeQuery(id+"F9.boolean.opBoolean","COPY",EDGE,{"derivedFrom":makeQuery(id+"F9.opExtrude","CAP_EDGE",EDGE,{"disambiguationData":[OSD([sQuery(id+"F8.wireOp",EDGE,"E21.right")])],"isStart":true})});
            var Q66;
            Q66=makeQuery(id+"F9.boolean.opBoolean","COPY",EDGE,{"derivedFrom":makeQuery(id+"F9.opExtrude","CAP_EDGE",EDGE,{"disambiguationData":[OSD([sQuery(id+"F8.wireOp",EDGE,"E21.bottom")])],"isStart":true})});
            var Q67;
            Q67=makeQuery(id+"F9.boolean.opBoolean","COPY",EDGE,{"derivedFrom":makeQuery(id+"F9.opExtrude","CAP_EDGE",EDGE,{"disambiguationData":[OSD([sQuery(id+"F8.wireOp",EDGE,"E21.left")])],"isStart":true})});
            var Q68;
            Q68=makeQuery(id+"F9.boolean.opBoolean","COPY",EDGE,{"derivedFrom":makeQuery(id+"F9.opExtrude","CAP_EDGE",EDGE,{"disambiguationData":[OSD([sQuery(id+"F8.wireOp",EDGE,"E21.top")])],"isStart":true})});
            var Q69;
            Q69=makeQuery(id+"F9.boolean.opBoolean","COPY",EDGE,{"derivedFrom":makeQuery(id+"F9.opExtrude","CAP_EDGE",EDGE,{"disambiguationData":[OSD([sQuery(id+"F8.wireOp",EDGE,"E19.bottom")])],"isStart":true})});
            var Q70;
            Q70=makeQuery(id+"F9.boolean.opBoolean","COPY",EDGE,{"derivedFrom":makeQuery(id+"F9.opExtrude","CAP_EDGE",EDGE,{"disambiguationData":[OSD([sQuery(id+"F8.wireOp",EDGE,"E19.left")])],"isStart":true})});
            var Q71;
            Q71=makeQuery(id+"F9.boolean.opBoolean","COPY",EDGE,{"derivedFrom":makeQuery(id+"F9.opExtrude","CAP_EDGE",EDGE,{"disambiguationData":[OSD([sQuery(id+"F8.wireOp",EDGE,"E19.top")])],"isStart":true})});
            var Q72;
            Q72=makeQuery(id+"F9.boolean.opBoolean","COPY",EDGE,{"derivedFrom":makeQuery(id+"F9.opExtrude","CAP_EDGE",EDGE,{"disambiguationData":[OSD([sQuery(id+"F8.wireOp",EDGE,"E19.right")])],"isStart":true})});
            var Q73;
            Q73=makeQuery(id+"F9.boolean.opBoolean","COPY",EDGE,{"derivedFrom":makeQuery(id+"F9.opExtrude","CAP_EDGE",EDGE,{"disambiguationData":[OSD([sQuery(id+"F8.wireOp",EDGE,"E17.right")])],"isStart":true})});
            var Q74;
            Q74=makeQuery(id+"F9.boolean.opBoolean","COPY",EDGE,{"derivedFrom":makeQuery(id+"F9.opExtrude","CAP_EDGE",EDGE,{"disambiguationData":[OSD([sQuery(id+"F8.wireOp",EDGE,"E17.bottom")])],"isStart":true})});
            var Q75;
            Q75=makeQuery(id+"F9.boolean.opBoolean","COPY",EDGE,{"derivedFrom":makeQuery(id+"F9.opExtrude","CAP_EDGE",EDGE,{"disambiguationData":[OSD([sQuery(id+"F8.wireOp",EDGE,"E17.top")])],"isStart":true})});
            var Q76;
            Q76=makeQuery(id+"F9.boolean.opBoolean","COPY",EDGE,{"derivedFrom":makeQuery(id+"F9.opExtrude","CAP_EDGE",EDGE,{"disambiguationData":[OSD([sQuery(id+"F8.wireOp",EDGE,"E17.left")])],"isStart":true})});
            var Q77;
            Q77=makeQuery(id+"F9.boolean.opBoolean","COPY",EDGE,{"derivedFrom":makeQuery(id+"F9.opExtrude","CAP_EDGE",EDGE,{"disambiguationData":[OSD([sQuery(id+"F8.wireOp",EDGE,"E15.left")])],"isStart":true})});
            var Q78;
            Q78=makeQuery(id+"F9.boolean.opBoolean","COPY",EDGE,{"derivedFrom":makeQuery(id+"F9.opExtrude","CAP_EDGE",EDGE,{"disambiguationData":[OSD([sQuery(id+"F8.wireOp",EDGE,"E15.bottom")])],"isStart":true})});
            var Q79;
            Q79=makeQuery(id+"F9.boolean.opBoolean","COPY",EDGE,{"derivedFrom":makeQuery(id+"F9.opExtrude","CAP_EDGE",EDGE,{"disambiguationData":[OSD([sQuery(id+"F8.wireOp",EDGE,"E15.top")])],"isStart":true})});
            var Q80;
            Q80=makeQuery(id+"F9.boolean.opBoolean","COPY",EDGE,{"derivedFrom":makeQuery(id+"F9.opExtrude","CAP_EDGE",EDGE,{"disambiguationData":[OSD([sQuery(id+"F8.wireOp",EDGE,"E15.right")])],"isStart":true})});
            var Q81;
            Q81=makeQuery(id+"F14.boolean.opBoolean","COPY",EDGE,{"derivedFrom":makeQuery(id+"F14.opExtrude","CAP_EDGE",EDGE,{"disambiguationData":[OSD([sQuery(id+"F13.wireOp",EDGE,"E27.top")])],"isStart":true})});
            var Q82;
            Q82=makeQuery(id+"F14.boolean.opBoolean","COPY",EDGE,{"derivedFrom":makeQuery(id+"F14.opExtrude","CAP_EDGE",EDGE,{"disambiguationData":[OSD([sQuery(id+"F13.wireOp",EDGE,"E27.bottom")])],"isStart":true})});
            var Q83;
            Q83=makeQuery(id+"F14.boolean.opBoolean","COPY",EDGE,{"derivedFrom":makeQuery(id+"F14.opExtrude","CAP_EDGE",EDGE,{"disambiguationData":[OSD([sQuery(id+"F13.wireOp",EDGE,"E27.right")])],"isStart":true})});
            var Q84;
            Q84=makeQuery(id+"F14.boolean.opBoolean","COPY",EDGE,{"derivedFrom":makeQuery(id+"F14.opExtrude","CAP_EDGE",EDGE,{"disambiguationData":[OSD([sQuery(id+"F13.wireOp",EDGE,"E27.left")])],"isStart":true})});
            var Q85;
            Q85=makeQuery(id+"F14.boolean.opBoolean","COPY",EDGE,{"derivedFrom":makeQuery(id+"F14.opExtrude","CAP_EDGE",EDGE,{"disambiguationData":[OSD([sQuery(id+"F13.wireOp",EDGE,"E28.left")])],"isStart":true})});
            var Q86;
            Q86=makeQuery(id+"F14.boolean.opBoolean","COPY",EDGE,{"derivedFrom":makeQuery(id+"F14.opExtrude","CAP_EDGE",EDGE,{"disambiguationData":[OSD([sQuery(id+"F13.wireOp",EDGE,"E28.bottom")])],"isStart":true})});
            var Q87;
            Q87=makeQuery(id+"F14.boolean.opBoolean","COPY",EDGE,{"derivedFrom":makeQuery(id+"F14.opExtrude","CAP_EDGE",EDGE,{"disambiguationData":[OSD([sQuery(id+"F13.wireOp",EDGE,"E28.top")])],"isStart":true})});
            var Q88;
            Q88=makeQuery(id+"F14.boolean.opBoolean","COPY",EDGE,{"derivedFrom":makeQuery(id+"F14.opExtrude","CAP_EDGE",EDGE,{"disambiguationData":[OSD([sQuery(id+"F13.wireOp",EDGE,"E28.right")])],"isStart":true})});
            var Q89;
            Q89=makeQuery(id+"F14.boolean.opBoolean","COPY",EDGE,{"derivedFrom":makeQuery(id+"F14.opExtrude","CAP_EDGE",EDGE,{"disambiguationData":[OSD([sQuery(id+"F13.wireOp",EDGE,"E29.top")])],"isStart":true})});
            var Q90;
            Q90=makeQuery(id+"F14.boolean.opBoolean","COPY",EDGE,{"derivedFrom":makeQuery(id+"F14.opExtrude","CAP_EDGE",EDGE,{"disambiguationData":[OSD([sQuery(id+"F13.wireOp",EDGE,"E29.right")])],"isStart":true})});
            var Q91;
            Q91=makeQuery(id+"F14.boolean.opBoolean","COPY",EDGE,{"derivedFrom":makeQuery(id+"F14.opExtrude","CAP_EDGE",EDGE,{"disambiguationData":[OSD([sQuery(id+"F13.wireOp",EDGE,"E29.bottom")])],"isStart":true})});
            var Q92;
            Q92=makeQuery(id+"F14.boolean.opBoolean","COPY",EDGE,{"derivedFrom":makeQuery(id+"F14.opExtrude","CAP_EDGE",EDGE,{"disambiguationData":[OSD([sQuery(id+"F13.wireOp",EDGE,"E29.left")])],"isStart":true})});
            var Q93;
            Q93=makeQuery(id+"F14.boolean.opBoolean","COPY",EDGE,{"derivedFrom":makeQuery(id+"F14.opExtrude","CAP_EDGE",EDGE,{"disambiguationData":[OSD([sQuery(id+"F13.wireOp",EDGE,"E30.top")])],"isStart":true})});
            var Q94;
            Q94=makeQuery(id+"F14.boolean.opBoolean","INTERSECT",EDGE,{"derivedFrom":[makeQuery(id+"F1.opExtrude","SWEPT_FACE",FACE,{"disambiguationData":[OSD([sQuery(id+"F0.wireOp",EDGE,"E0.right")])]}),makeQuery(id+"F14.opExtrude","SWEPT_FACE",FACE,{"disambiguationData":[OSD([sQuery(id+"F13.wireOp",EDGE,"E30.bottom")])]})]});
            var Q95;
            Q95=makeQuery(id+"F14.boolean.opBoolean","COPY",EDGE,{"derivedFrom":makeQuery(id+"F14.opExtrude","CAP_EDGE",EDGE,{"disambiguationData":[OSD([sQuery(id+"F13.wireOp",EDGE,"E30.right")])],"isStart":true})});
            var Q96;
            Q96=makeQuery(id+"F14.boolean.opBoolean","COPY",EDGE,{"derivedFrom":makeQuery(id+"F14.opExtrude","CAP_EDGE",EDGE,{"disambiguationData":[OSD([sQuery(id+"F13.wireOp",EDGE,"E30.bottom")])],"isStart":true})});
            var Q97;
            Q97=makeQuery(id+"F14.boolean.opBoolean","COPY",EDGE,{"derivedFrom":makeQuery(id+"F14.opExtrude","CAP_EDGE",EDGE,{"disambiguationData":[OSD([sQuery(id+"F13.wireOp",EDGE,"E30.left")])],"isStart":true})});
            fillet(context, id + "F15", {"entities" : qUnion([Q0, Q1, Q2, Q3, Q4, Q5, Q6, Q7, Q8, Q9, Q10, Q11, Q12, Q13, Q14, Q15, Q16, Q17, Q18, Q19, Q20, Q21, Q22, Q23, Q24, Q25, Q26, Q27, Q28, Q29, Q30, Q31, Q32, Q33, Q34, Q35, Q36, Q37, Q38, Q39, Q40, Q41, Q42, Q43, Q44, Q45, Q46, Q47, Q48, Q49, Q50, Q51, Q52, Q53, Q54, Q55, Q56, Q57, Q58, Q59, Q60, Q61, Q62, Q63, Q64, Q65, Q66, Q67, Q68, Q69, Q70, Q71, Q72, Q73, Q74, Q75, Q76, Q77, Q78, Q79, Q80, Q81, Q82, Q83, Q84, Q85, Q86, Q87, Q88, Q89, Q90, Q91, Q92, Q93, Q94, Q95, Q96, Q97]), "radius" : .5 * mm, "tangentPropagation" : true, "allowEdgeOverflow" : false});
        }
        {
            var Q0;
            Q0=makeQuery(id+"F1.opExtrude","SWEPT_FACE",FACE,{"disambiguationData":[OSD([sQuery(id+"F0.wireOp",EDGE,"E1.right")])]});
            var sketch = newSketch(context, id + "F16", { "sketchPlane" : qUnion([Q0])});
            skText(sketch, "E31", { "text": "idk", "fontName": "OpenSans-Bold.ttf"});
            const initialGuessF16  = {"E31": [-0.00696, -0.03927, 1, 0, 0.00675]};
            skSetInitialGuess(sketch, initialGuessF16);
            skSolve(sketch);
        }
        {
            var Q0;
            Q0=qSketchRegion(id+"F16",true);
            extrude(context, id + "F17", {"entities" : qUnion([Q0]), "operationType" : NewBodyOperationType.REMOVE, "oppositeDirection" : true, "depth" : .75 * mm, "offsetDistance" : 25 * mm});
        }
        {
            var Q0;
            Q0=makeQuery(id+"F0.imprint","IMPRINT",FACE,{"disambiguationData":[TD([[makeQuery(id+"F0.imprint","IMPRINT",EDGE,{"derivedFrom":sQuery(id+"F0.wireOp",EDGE,"E3.bottom")}),-1.0]])]});
            extrude(context, id + "F18", {"entities" : qUnion([Q0]), "operationType" : NewBodyOperationType.ADD, "oppositeDirection" : true, "depth" : 3 * mm, "offsetDistance" : 25 * mm});
        }
    });
